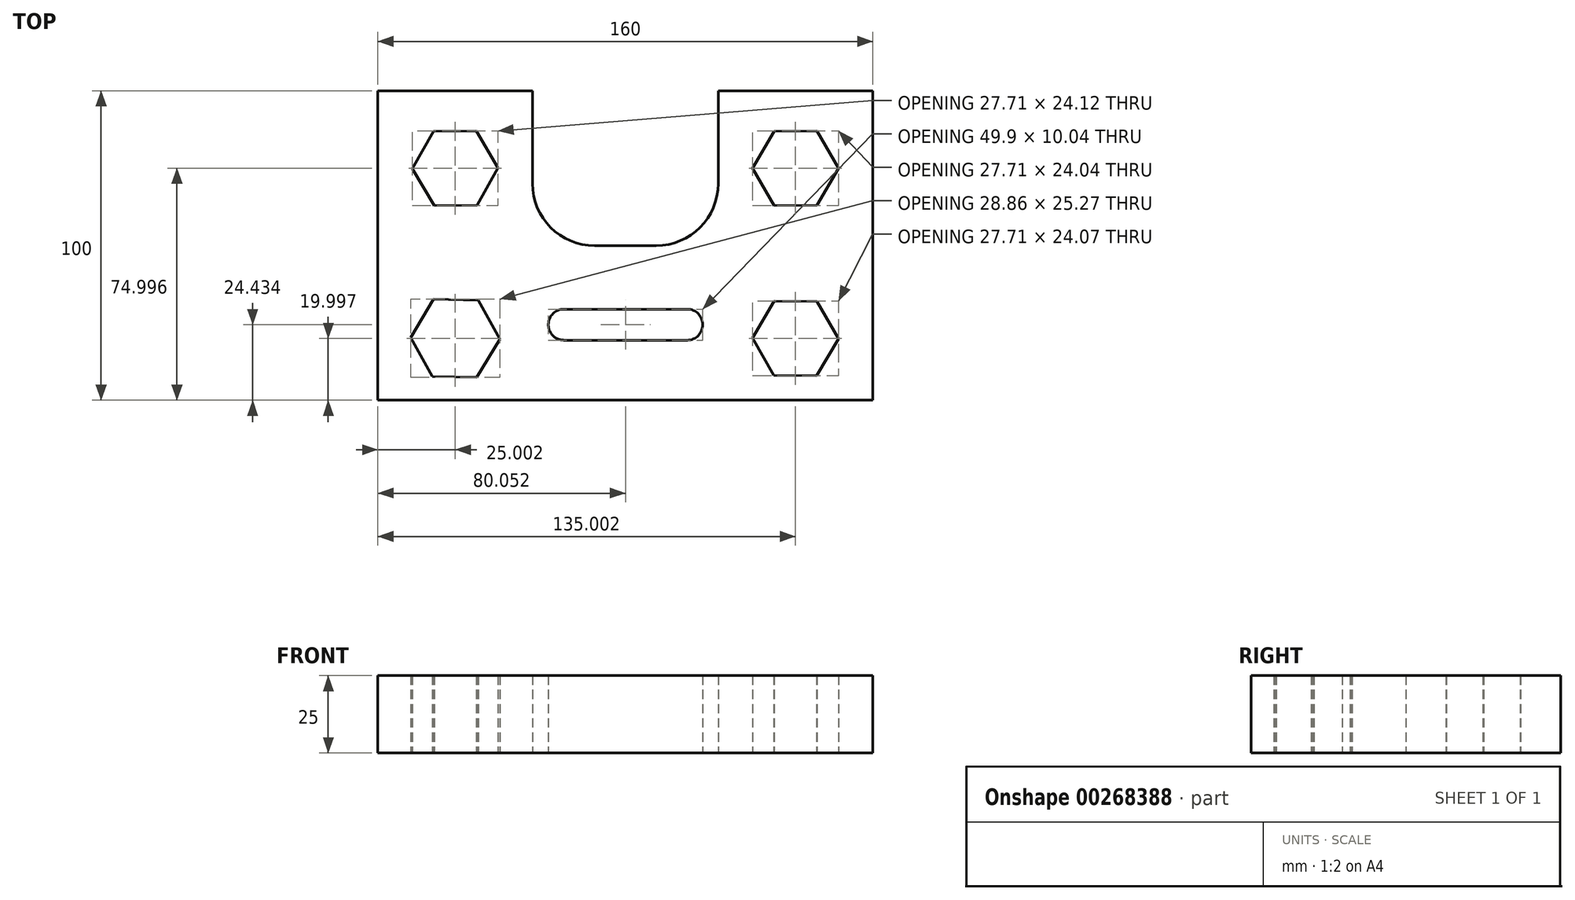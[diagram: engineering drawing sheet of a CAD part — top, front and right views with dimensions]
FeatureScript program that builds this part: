
annotation { "Feature Type Name" : "Feature", "Feature Type Description" : "" }
export const myFeature = defineFeature(function(context is Context, id is Id, definition is map)
    precondition{}
    {
        {
            var Q0;
            Q0=qCreatedBy(makeId("Top.planeOp"),FACE);
            var sketch = newSketch(context, id + "F0", { "sketchPlane" : qUnion([Q0])});
            skLineSegment(sketch, "E0", {"start": v(-110.87, -42.31) * mm, "end": v(49.13, -42.31) * mm});
            skLineSegment(sketch, "E1", {"start": v(-110.87, -42.31) * mm, "end": v(-110.87, 57.69) * mm});
            skLineSegment(sketch, "E2", {"start": v(49.13, -42.31) * mm, "end": v(49.13, 57.69) * mm});
            skLineSegment(sketch, "E3", {"start": v(49.13, 57.69) * mm, "end": v(-0.87, 57.69) * mm});
            skLineSegment(sketch, "E4", {"start": v(-110.87, 57.69) * mm, "end": v(-60.87, 57.69) * mm});
            skLineSegment(sketch, "E5", {"start": v(-60.87, 57.69) * mm, "end": v(-60.87, 27.69) * mm});
            skLineSegment(sketch, "E6", {"start": v(-40.87, 7.69) * mm, "end": v(-20.87, 7.69) * mm});
            skLineSegment(sketch, "E7", {"start": v(-0.87, 27.69) * mm, "end": v(-0.87, 57.69) * mm});
            skPoint(sketch, "E8.visualSharp", {"position": v(-60.87, 7.69) * mm});
            skArc(sketch, "E8.filletArc", {"start": v(-60.87, 27.69) * mm, "mid": v(-55, 13.54) * mm, "end": v(-40.87, 7.69) * mm});
            skPoint(sketch, "E9.visualSharp", {"position": v(-0.87, 7.69) * mm});
            skArc(sketch, "E9.filletArc", {"start": v(-20.87, 7.69) * mm, "mid": v(-6.73, 13.54) * mm, "end": v(-0.87, 27.69) * mm});
            skLineSegment(sketch, "E10.trimOffspring", {"start": v(-60.87, 57.69) * mm, "end": v(-110.87, 57.69) * mm});
            skLineSegment(sketch, "E11", {"start": v(49.13, -42.31) * mm, "end": v(49.13, -22.31) * mm});
            skLineSegment(sketch, "E12", {"start": v(49.13, -42.31) * mm, "end": v(24.13, -42.31) * mm});
            skLineSegment(sketch, "E13", {"start": v(24.13, -42.31) * mm, "end": v(24.13, -22.31) * mm, "construction": true});
            skCircle(sketch, "E14.cCircle", {"center": v(24.13, -22.31) * mm, "radius": 12 * mm});
            skLineSegment(sketch, "E14.0", {"start": v(10.28, -22.24) * mm, "end": v(17.27, -10.28) * mm});
            skLineSegment(sketch, "E14.1", {"start": v(17.27, -10.28) * mm, "end": v(31.12, -10.35) * mm});
            skLineSegment(sketch, "E14.2", {"start": v(31.12, -10.35) * mm, "end": v(37.99, -22.39) * mm});
            skLineSegment(sketch, "E14.3", {"start": v(37.99, -22.39) * mm, "end": v(31, -34.35) * mm});
            skLineSegment(sketch, "E14.4", {"start": v(31, -34.35) * mm, "end": v(17.14, -34.28) * mm});
            skLineSegment(sketch, "E14.5", {"start": v(17.14, -34.28) * mm, "end": v(10.28, -22.24) * mm});
            skPoint(sketch, "E14.0.midPoint", {"position": v(13.77, -16.26) * mm});
            skLineSegment(sketch, "E15", {"start": v(49.13, -22.31) * mm, "end": v(49.13, 32.69) * mm});
            skLineSegment(sketch, "E16", {"start": v(49.13, 32.69) * mm, "end": v(24.13, 32.69) * mm, "construction": true});
            skLineSegment(sketch, "E17", {"start": v(-110.87, -42.31) * mm, "end": v(-85.87, -42.31) * mm});
            skLineSegment(sketch, "E18", {"start": v(-110.87, -42.31) * mm, "end": v(-110.87, -22.31) * mm});
            skLineSegment(sketch, "E19", {"start": v(-110.87, -22.31) * mm, "end": v(-85.87, -22.31) * mm, "construction": true});
            skCircle(sketch, "E20.cCircle", {"center": v(-85.87, -22.31) * mm, "radius": 12.5 * mm});
            skLineSegment(sketch, "E20.0", {"start": v(-100.3, -22.03) * mm, "end": v(-92.84, -9.68) * mm});
            skLineSegment(sketch, "E20.1", {"start": v(-92.84, -9.68) * mm, "end": v(-78.41, -9.96) * mm});
            skLineSegment(sketch, "E20.2", {"start": v(-78.41, -9.96) * mm, "end": v(-71.44, -22.6) * mm});
            skLineSegment(sketch, "E20.3", {"start": v(-71.44, -22.6) * mm, "end": v(-78.9, -34.95) * mm});
            skLineSegment(sketch, "E20.4", {"start": v(-78.9, -34.95) * mm, "end": v(-93.32, -34.67) * mm});
            skLineSegment(sketch, "E20.5", {"start": v(-93.32, -34.67) * mm, "end": v(-100.3, -22.03) * mm});
            skPoint(sketch, "E20.0.midPoint", {"position": v(-96.57, -15.86) * mm});
            skLineSegment(sketch, "E21", {"start": v(-110.87, -22.31) * mm, "end": v(-110.87, 32.69) * mm});
            skLineSegment(sketch, "E22", {"start": v(-110.87, 32.69) * mm, "end": v(-85.87, 32.69) * mm});
            skCircle(sketch, "E23.cCircle", {"center": v(-85.87, 32.69) * mm, "radius": 12 * mm});
            skLineSegment(sketch, "E23.0", {"start": v(-92.69, 20.63) * mm, "end": v(-99.72, 32.56) * mm});
            skLineSegment(sketch, "E23.1", {"start": v(-99.72, 32.56) * mm, "end": v(-92.9, 44.62) * mm});
            skLineSegment(sketch, "E23.2", {"start": v(-92.9, 44.62) * mm, "end": v(-79.05, 44.75) * mm});
            skLineSegment(sketch, "E23.3", {"start": v(-79.05, 44.75) * mm, "end": v(-72.01, 32.81) * mm});
            skLineSegment(sketch, "E23.4", {"start": v(-72.01, 32.81) * mm, "end": v(-78.83, 20.75) * mm});
            skLineSegment(sketch, "E23.5", {"start": v(-78.83, 20.75) * mm, "end": v(-92.69, 20.63) * mm});
            skPoint(sketch, "E23.0.midPoint", {"position": v(-96.2, 26.6) * mm});
            skCircle(sketch, "E24.cCircle", {"center": v(24.13, 32.69) * mm, "radius": 12 * mm});
            skLineSegment(sketch, "E24.0", {"start": v(17.24, 20.67) * mm, "end": v(10.28, 32.65) * mm});
            skLineSegment(sketch, "E24.1", {"start": v(10.28, 32.65) * mm, "end": v(17.17, 44.67) * mm});
            skLineSegment(sketch, "E24.2", {"start": v(17.17, 44.67) * mm, "end": v(31.03, 44.7) * mm});
            skLineSegment(sketch, "E24.3", {"start": v(31.03, 44.7) * mm, "end": v(37.99, 32.73) * mm});
            skLineSegment(sketch, "E24.4", {"start": v(37.99, 32.73) * mm, "end": v(31.1, 20.7) * mm});
            skLineSegment(sketch, "E24.5", {"start": v(31.1, 20.7) * mm, "end": v(17.24, 20.67) * mm});
            skPoint(sketch, "E24.0.midPoint", {"position": v(13.76, 26.66) * mm});
            skLineSegment(sketch, "E25", {"start": v(-110.87, -42.31) * mm, "end": v(-55.87, -42.31) * mm});
            skLineSegment(sketch, "E26", {"start": v(-50.77, -22.9) * mm, "end": v(-10.87, -22.9) * mm});
            skLineSegment(sketch, "E27", {"start": v(-55.77, -17.8) * mm, "end": v(-55.77, -17.76) * mm});
            skLineSegment(sketch, "E28", {"start": v(-50.77, -12.86) * mm, "end": v(-10.87, -12.86) * mm});
            skLineSegment(sketch, "E29", {"start": v(-5.87, -17.86) * mm, "end": v(-5.87, -17.9) * mm});
            skPoint(sketch, "E30.visualSharp", {"position": v(-55.67, -12.86) * mm});
            skArc(sketch, "E30.filletArc", {"start": v(-50.77, -12.86) * mm, "mid": v(-54.27, -14.29) * mm, "end": v(-55.77, -17.76) * mm});
            skPoint(sketch, "E31.visualSharp", {"position": v(-55.87, -22.9) * mm});
            skArc(sketch, "E31.filletArc", {"start": v(-55.77, -17.8) * mm, "mid": v(-54.34, -21.4) * mm, "end": v(-50.77, -22.9) * mm});
            skPoint(sketch, "E32.visualSharp", {"position": v(-5.87, -12.86) * mm});
            skArc(sketch, "E32.filletArc", {"start": v(-5.87, -17.86) * mm, "mid": v(-7.33, -14.32) * mm, "end": v(-10.87, -12.86) * mm});
            skPoint(sketch, "E33.visualSharp", {"position": v(-5.87, -22.9) * mm});
            skArc(sketch, "E33.filletArc", {"start": v(-10.87, -22.9) * mm, "mid": v(-7.33, -21.43) * mm, "end": v(-5.87, -17.9) * mm});
            skSolve(sketch);
        }
        {
            var Q0;
            Q0 = qSketchRegion(id + "F0", true);
            extrude(context, id + "F1", {"entities" : qUnion([Q0]), "depth" : 25 * mm});
        }
    });
